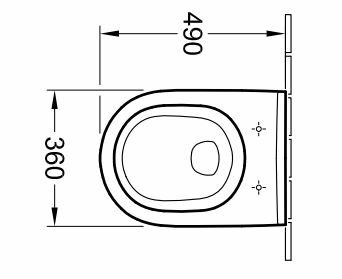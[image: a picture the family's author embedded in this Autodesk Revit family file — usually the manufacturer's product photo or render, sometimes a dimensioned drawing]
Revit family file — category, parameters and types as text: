
# Revit family: Combi-Pack 5656HR
name_source: partatom
category: Plumbing Fixtures
revit_build: Autodesk Revit 2016 (Build: 20150714_1515(x64)
units: mm (PartAtom-declared; Revit-internal decimal feet)

## family parameters
Always vertical = Yes
Cut with Voids When Loaded = No
OmniClass Number = 23.45.00.00
OmniClass Title = Sanitary, Laundry, and Cleaning Equipment
Part Type = Normal
Room Calculation Point = No
Round Connector Dimension = Use Diameter
Shared = No
Work Plane-Based = No

## types (1)
- Combi-Pack 5656HR
    Depth = 530 mm  [stored 1.73885 ft]
    Height = 400 mm  [stored 1.31234 ft]
    Manufacturer = Villeroy and Boch
    Material = Ceramic White
    Model = Combi-Pack 5656HR
    URL = https://pro.villeroy-boch.com
    Width = 370 mm  [stored 1.21391 ft]

note: [stored X ft] marks values corroborated as IEEE doubles in the binary element streams (Revit-internal decimal feet)

## geometry (parser evidence)
native form markers: Sweep x3
no freeform markers — native parametric forms only
